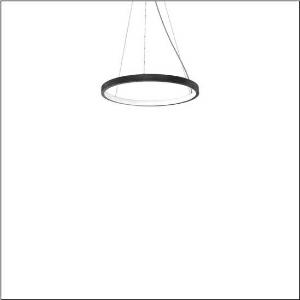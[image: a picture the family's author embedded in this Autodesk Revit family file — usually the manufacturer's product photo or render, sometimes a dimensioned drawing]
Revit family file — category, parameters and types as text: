
# Revit family: silica_21_ring-i_5pjbi1d1104a
name_source: partatom
category: Lighting Fixtures
units: mm (PartAtom-declared; Revit-internal decimal feet)

## family parameters
Cut with Voids When Loaded = No
Host = Face
Light Source = No
Part Type = Normal
Room Calculation Point = No
Round Connector Dimension = Use Diameter
Shared = No

## types (1)
- Silica 21 Ring-I (1 x LED, 3430 lm, 60 W, 3000K)
    Apparent Load = 60 VA
    CIE Flux Codes = 22 48 76 50 101
    Color Rendering = 80
    Color Temperature = 3000K
    Default Elevation = 1800 mm
    Description = Silica 21 Ring-I, suspended luminaire, of PMMA, frosted, light emission: inner ring side luminous distribution, primary light characteristic: symmetric, installation type: suspended mounting, LED, rated luminous flux: 3.430lm, luminous efficacy: 57lm/W, light colour: 830, colour temperature: 3000K, control gear: DALI 2, with terminal, 5-pole, mains connection: 230V, AC/DC, 0/50..60Hz, rated input power: 60W, housing, of extruded aluminium section, jet black (RAL 9005), diameter: 610mm, ceiling canopy, jet black (RAL 9005), protection rating (lamp compartment): IP40, insulation class (complete): insulation class I (protective earthing), certification: CE, impact resistance: IK02, permissible operating ambient temperature: 0..+35°C, packaging unit: 1 piece
    Height = 48 mm  [stored 0.15748 ft]
    Lamp = 1 x LED
    Lamp Light Flux = 3430 lm
    Lamp Power = 60 W
    Lamp count = 1
    Length = 610 mm
    Luminous efficacy = 57 lm/W
    Manufacturer = Siteco
    ModVariant = No
    Model = 5PJBI1D1104A
    Mounting Place = Ceiling
    Mounting Type = Pendant
    Number of Poles = 1
    OnlyDefault = Yes
    Power Factor = 1
    Product Name = Silica 21 Ring-I
    Product group = suspended luminaire
    ProductGroupID = 904
    Protection Class = Protection class I
    Protection Degree = IP 40
    RLX_Detail_Level = 1
    RLX_Emergency_Light_Flux = 0 lm
    RLX_Emergency_Type = 0
    RLX_Emergency_Type_DB = No
    RlxData = <blob elided: 12341 chars, md5=dcfd26dc>
    Socket = socket
    Standby Power = 0 W
    System Light Flux = 3430 lm
    System Power = 60 W
    Type Comments = Product without accessories
    Type Image = l_1258361.jpg
    URL = http://relux.com
    VarID = ---
    Voltage = 0 V
    Weight = 0.00 kg
    Width = 0 mm  [stored 0 ft]

note: [stored X ft] marks values corroborated as IEEE doubles in the binary element streams (Revit-internal decimal feet)

## geometry (parser evidence)
native form markers: Sweep x15
no freeform markers — native parametric forms only
